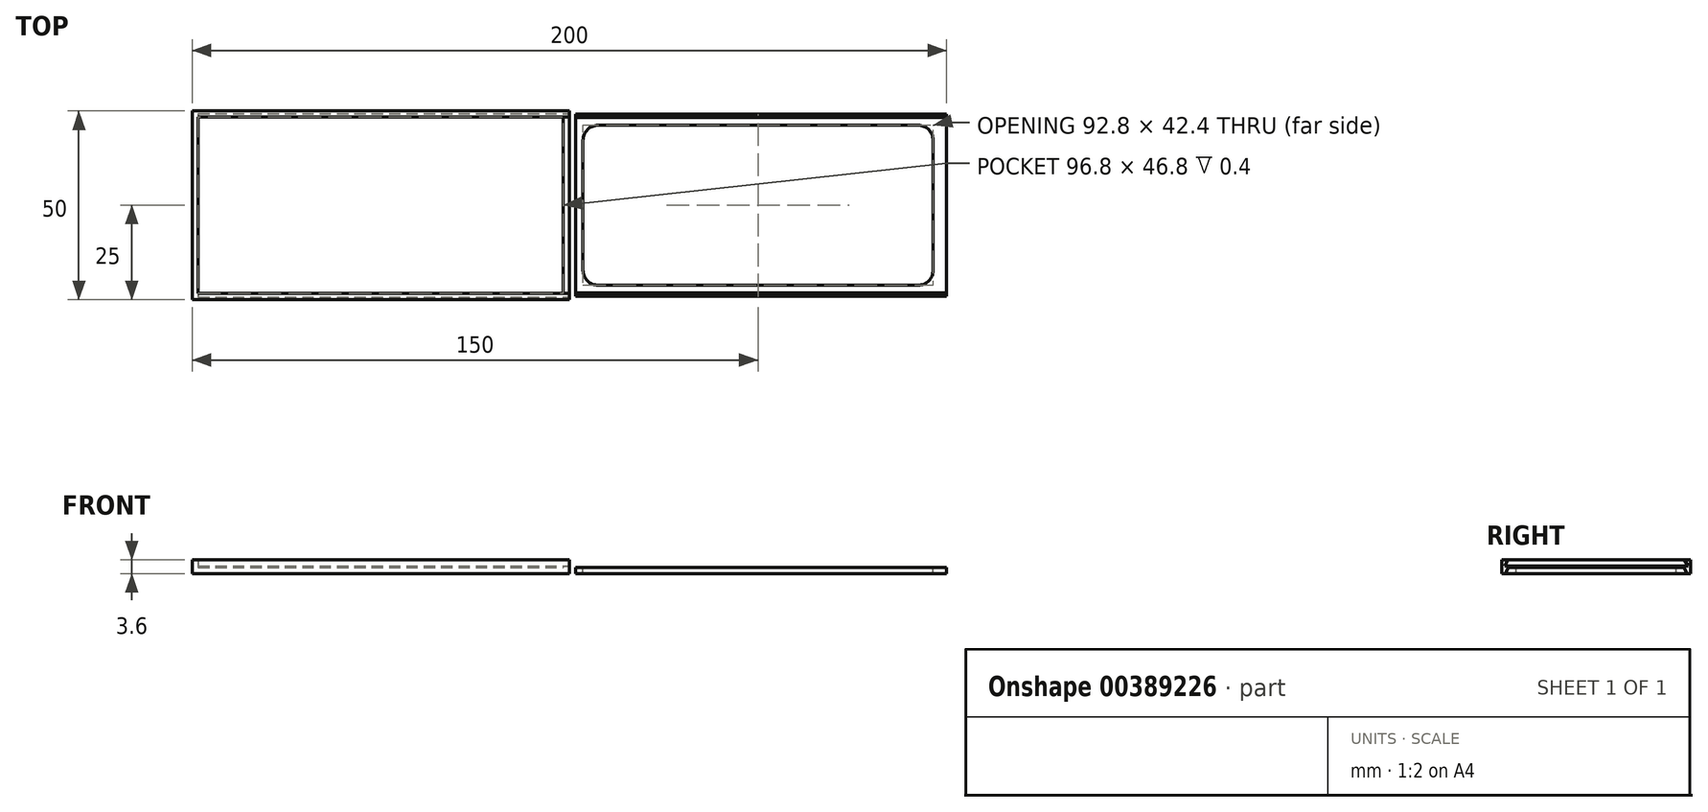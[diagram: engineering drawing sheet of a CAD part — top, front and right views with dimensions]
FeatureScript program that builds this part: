
annotation { "Feature Type Name" : "Feature", "Feature Type Description" : "" }
export const myFeature = defineFeature(function(context is Context, id is Id, definition is map)
    precondition{}
    {
        {
            assignVariable(context, id + "F0", {"name" : "Height", "anyValue" : 3.6});
        }
        {
            assignVariable(context, id + "F1", {"name" : "Length", "anyValue" : 100});
        }
        {
            assignVariable(context, id + "F2", {"name" : "WallThickness", "anyValue" : 1.6});
        }
        {
            var Q0;
            Q0=qCreatedBy(makeId("Top.planeOp"),FACE);
            var sketch = newSketch(context, id + "F3", { "sketchPlane" : qUnion([Q0])});
            skLineSegment(sketch, "E0", {"start": v(0, 0) * mm, "end": v(100, 0) * mm});
            skLineSegment(sketch, "E1", {"start": v(100, 0) * mm, "end": v(100, 50) * mm});
            skLineSegment(sketch, "E2", {"start": v(100, 50) * mm, "end": v(0, 50) * mm});
            skLineSegment(sketch, "E3", {"start": v(0, 50) * mm, "end": v(0, 0) * mm});
            skLineSegment(sketch, "E4.0", {"start": v(1.6, 1.6) * mm, "end": v(98.4, 1.6) * mm});
            skLineSegment(sketch, "E4.1", {"start": v(1.6, 48.4) * mm, "end": v(1.6, 1.6) * mm});
            skLineSegment(sketch, "E4.2", {"start": v(98.4, 48.4) * mm, "end": v(1.6, 48.4) * mm});
            skLineSegment(sketch, "E4.3", {"start": v(98.4, 1.6) * mm, "end": v(98.4, 48.4) * mm});
            skLineSegment(sketch, "E5", {"start": v(98.4, 1.6) * mm, "end": v(100, 1.6) * mm});
            skLineSegment(sketch, "E6", {"start": v(98.4, 48.4) * mm, "end": v(100, 48.4) * mm});
            skLineSegment(sketch, "E7", {"start": v(50, 50) * mm, "end": v(50, 0) * mm, "construction": true});
            skLineSegment(sketch, "E8", {"start": v(50.8, 1.6) * mm, "end": v(50.8, 48.4) * mm});
            skLineSegment(sketch, "E9.MirrorCS", {"start": v(49.2, 1.6) * mm, "end": v(49.2, 48.4) * mm});
            skSolve(sketch);
        }
        {
            var Q0;
            Q0=makeQuery(id+"F3.imprint","IMPRINT",FACE,{"disambiguationData":[TD([[makeQuery(id+"F3.imprint","IMPRINT",EDGE,{"derivedFrom":sQuery(id+"F3.wireOp",EDGE,"E0")}),1.0]])]});
            extrude(context, id + "F4", {"entities" : qUnion([Q0]), "depth" : (getVariable(context, 'Height')) * mm});
        }
        {
            var Q0;
            Q0=makeQuery(id+"F3.imprint","IMPRINT",FACE,{"disambiguationData":[TD([[makeQuery(id+"F3.imprint","IMPRINT",EDGE,{"derivedFrom":sQuery(id+"F3.wireOp",EDGE,"E4.0")}),1.0]])]});
            extrude(context, id + "F5", {"entities" : qUnion([Q0]), "operationType" : NewBodyOperationType.ADD, "depth" : (getVariable(context, 'WallThickness')) * mm});
        }
        {
            var Q0;
            Q0=makeQuery(id+"F3.imprint","IMPRINT",FACE,{"disambiguationData":[TD([[makeQuery(id+"F3.imprint","IMPRINT",EDGE,{"derivedFrom":sQuery(id+"F3.wireOp",EDGE,"E4.3")}),-1.0]])]});
            extrude(context, id + "F6", {"entities" : qUnion([Q0]), "operationType" : NewBodyOperationType.ADD, "depth" : (getVariable(context, 'Height') - getVariable(context, 'WallThickness')) * mm});
        }
        {
            var Q0;
            {var subQ0=sQuery(id+"F3.wireOp",EDGE,"E1");Q0=makeQuery(id+"F6.boolean.opBoolean","MERGE",FACE,{"derivedFrom":[makeQuery(id+"F4.opExtrude","SWEPT_FACE",FACE,{"disambiguationData":[OSD([subQ0]),TDD([makeQuery(id+"F3.imprint","IMPRINT",EDGE,{"disambiguationData":[TD([[makeQuery(id+"F3.imprint","INTERSECT",VERTEX,{"derivedFrom":[sQuery(id+"F3.wireOp",EDGE,"E0"),subQ0]}),-1.0]])],"derivedFrom":subQ0})])]}),makeQuery(id+"F4.opExtrude","SWEPT_FACE",FACE,{"disambiguationData":[OSD([subQ0]),TDD([makeQuery(id+"F3.imprint","IMPRINT",EDGE,{"disambiguationData":[TD([[makeQuery(id+"F3.imprint","INTERSECT",VERTEX,{"derivedFrom":[subQ0,sQuery(id+"F3.wireOp",EDGE,"E2")]}),1.0]])],"derivedFrom":subQ0})])]}),makeQuery(id+"F6.opExtrude","SWEPT_FACE",FACE,{"disambiguationData":[OSD([subQ0])]})]});}
            var sketch = newSketch(context, id + "F7", { "sketchPlane" : qUnion([Q0])});
            skLineSegment(sketch, "E10.0", {"start": v(1.6, 2) * mm, "end": v(48.4, 2) * mm});
            skLineSegment(sketch, "E10.1", {"start": v(0, 3.6) * mm, "end": v(1.6, 3.6) * mm, "construction": true});
            skLineSegment(sketch, "E10.2", {"start": v(48.4, 3.6) * mm, "end": v(50, 3.6) * mm, "construction": true});
            skLineSegment(sketch, "E10.3", {"start": v(50, 3.6) * mm, "end": v(50, 0) * mm, "construction": true});
            skLineSegment(sketch, "E10.4", {"start": v(0, 3.6) * mm, "end": v(0, 0) * mm, "construction": true});
            skLineSegment(sketch, "E11", {"start": v(1.6, 3.6) * mm, "end": v(0.68, 2) * mm});
            skLineSegment(sketch, "E12", {"start": v(0.68, 2) * mm, "end": v(1.6, 2) * mm});
            skPoint(sketch, "E13", {"position": v(25, 2) * mm});
            skLineSegment(sketch, "E14", {"start": v(25, 104.43) * mm, "end": v(25, 92.5) * mm, "construction": true});
            skLineSegment(sketch, "E15.MirrorCS", {"start": v(48.4, 3.6) * mm, "end": v(49.32, 2) * mm});
            skLineSegment(sketch, "E16.MirrorCS", {"start": v(49.32, 2) * mm, "end": v(48.4, 2) * mm});
            skLineSegment(sketch, "E17", {"start": v(1.6, 3.6) * mm, "end": v(48.4, 3.6) * mm});
            skLineSegment(sketch, "E18", {"start": v(0.88, 2) * mm, "end": v(1.8, 3.6) * mm});
            skLineSegment(sketch, "E19.MirrorCS", {"start": v(49.12, 2) * mm, "end": v(48.2, 3.6) * mm});
            skSolve(sketch);
        }
        {
            var Q0;
            Q0=makeQuery(id+"F7.imprint","IMPRINT",FACE,{"disambiguationData":[TD([[makeQuery(id+"F7.imprint","IMPRINT",EDGE,{"derivedFrom":sQuery(id+"F7.wireOp",EDGE,"E11")}),1.0]])]});
            var Q1;
            Q1=makeQuery(id+"F7.imprint","IMPRINT",FACE,{"disambiguationData":[TD([[makeQuery(id+"F7.imprint","IMPRINT",EDGE,{"derivedFrom":sQuery(id+"F7.wireOp",EDGE,"E15.MirrorCS")}),-1.0]])]});
            var Q2;
            {var subQ0=sQuery(id+"F7.wireOp",EDGE,"E12");var subQ3=sQuery(id+"F7.wireOp",EDGE,"E18");var subQ4=makeQuery(id+"F7.imprint","INTERSECT",VERTEX,{"derivedFrom":[subQ0,subQ3]});Q2=makeQuery(id+"F7.imprint","IMPRINT",FACE,{"disambiguationData":[TD([[makeQuery(id+"F7.imprint","IMPRINT",EDGE,{"disambiguationData":[TD([[subQ4,-1.0]])],"derivedFrom":subQ3}),-1.0]])]});}
            var Q3;
            {var subQ0=sQuery(id+"F7.wireOp",EDGE,"E16.MirrorCS");var subQ3=sQuery(id+"F7.wireOp",EDGE,"E19.MirrorCS");var subQ4=makeQuery(id+"F7.imprint","INTERSECT",VERTEX,{"derivedFrom":[subQ0,subQ3]});Q3=makeQuery(id+"F7.imprint","IMPRINT",FACE,{"disambiguationData":[TD([[makeQuery(id+"F7.imprint","IMPRINT",EDGE,{"disambiguationData":[TD([[subQ4,-1.0]])],"derivedFrom":subQ3}),1.0]])]});}
            extrude(context, id + "F8", {"entities" : qUnion([Q0, Q1, Q2, Q3]), "operationType" : NewBodyOperationType.REMOVE, "oppositeDirection" : true, "depth" : (getVariable(context, 'Length') - getVariable(context, 'WallThickness')) * mm});
        }
        {
            var Q0;
            Q0=makeQuery(id+"F7.imprint","IMPRINT",FACE,{"disambiguationData":[TD([[makeQuery(id+"F7.imprint","IMPRINT",EDGE,{"derivedFrom":sQuery(id+"F7.wireOp",EDGE,"E10.0")}),1.0]])]});
            var Q1;
            {var subQ0=sQuery(id+"F7.wireOp",EDGE,"E12");var subQ3=sQuery(id+"F7.wireOp",EDGE,"E18");var subQ4=makeQuery(id+"F7.imprint","INTERSECT",VERTEX,{"derivedFrom":[subQ0,subQ3]});Q1=makeQuery(id+"F7.imprint","IMPRINT",FACE,{"disambiguationData":[TD([[makeQuery(id+"F7.imprint","IMPRINT",EDGE,{"disambiguationData":[TD([[subQ4,-1.0]])],"derivedFrom":subQ3}),-1.0]])]});}
            var Q2;
            {var subQ0=sQuery(id+"F7.wireOp",EDGE,"E16.MirrorCS");var subQ3=sQuery(id+"F7.wireOp",EDGE,"E19.MirrorCS");var subQ4=makeQuery(id+"F7.imprint","INTERSECT",VERTEX,{"derivedFrom":[subQ0,subQ3]});Q2=makeQuery(id+"F7.imprint","IMPRINT",FACE,{"disambiguationData":[TD([[makeQuery(id+"F7.imprint","IMPRINT",EDGE,{"disambiguationData":[TD([[subQ4,-1.0]])],"derivedFrom":subQ3}),1.0]])]});}
            extrude(context, id + "F9", {"entities" : qUnion([Q0, Q1, Q2]), "depth" : (getVariable(context, 'Length')) * mm, "hasSecondDirection" : true, "secondDirectionOppositeDirection" : false, "secondDirectionDepth" : (getVariable(context, 'WallThickness')) * mm});
        }
        {
            var Q0;
            Q0=makeQuery(id+"F9.opExtrude","SWEPT_BODY",BODY,{"disambiguationData":[OSD([sQuery(id+"F7.wireOp",EDGE,"E10.0"),sQuery(id+"F7.wireOp",EDGE,"E12"),sQuery(id+"F7.wireOp",EDGE,"E16.MirrorCS"),sQuery(id+"F7.wireOp",EDGE,"E17"),sQuery(id+"F7.wireOp",EDGE,"E18"),sQuery(id+"F7.wireOp",EDGE,"E19.MirrorCS")])]});
            transform(context, id + "F10", {"entities" : qUnion([Q0]), "transformType" : TransformType.TRANSLATION_3D, "dx" : 0 * mm, "dy" : 0 * mm, "dz" : (-getVariable(context, 'Height') + getVariable(context, 'WallThickness')) * mm, "makeCopy" : false});
        }
        {
            var Q0;
            Q0=makeQuery(id+"F9.opExtrude","SWEPT_FACE",FACE,{"disambiguationData":[OSD([sQuery(id+"F7.wireOp",EDGE,"E17")])]});
            var sketch = newSketch(context, id + "F11", { "sketchPlane" : qUnion([Q0])});
            skLineSegment(sketch, "E20.0", {"start": v(200, 1.8) * mm, "end": v(200, 48.2) * mm, "construction": true});
            skLineSegment(sketch, "E20.1", {"start": v(200, 48.2) * mm, "end": v(101.6, 48.2) * mm, "construction": true});
            skLineSegment(sketch, "E20.2", {"start": v(200, 1.8) * mm, "end": v(101.6, 1.8) * mm, "construction": true});
            skLineSegment(sketch, "E20.3", {"start": v(101.6, 1.8) * mm, "end": v(101.6, 48.2) * mm, "construction": true});
            skLineSegment(sketch, "E21", {"start": v(196.4, 46.2) * mm, "end": v(196.4, 3.8) * mm});
            skLineSegment(sketch, "E22", {"start": v(196.4, 3.8) * mm, "end": v(103.6, 3.8) * mm});
            skLineSegment(sketch, "E23", {"start": v(103.6, 3.8) * mm, "end": v(103.6, 46.2) * mm});
            skLineSegment(sketch, "E24", {"start": v(103.6, 46.2) * mm, "end": v(196.4, 46.2) * mm});
            skPoint(sketch, "E25", {"position": v(196.4, 25) * mm});
            skPoint(sketch, "E26", {"position": v(200, 25) * mm});
            skSolve(sketch);
        }
        {
            var Q0;
            Q0=makeQuery(id+"F4.opExtrude","SWEPT_FACE",FACE,{"disambiguationData":[OSD([sQuery(id+"F3.wireOp",EDGE,"E0")])]});
            var sketch = newSketch(context, id + "F12", { "sketchPlane" : qUnion([Q0])});
            skLineSegment(sketch, "E27.0", {"start": v(0, 3.6) * mm, "end": v(0, 0) * mm, "construction": true});
            skLineSegment(sketch, "E27.1", {"start": v(0, 3.6) * mm, "end": v(100, 3.6) * mm, "construction": true});
            skLineSegment(sketch, "E27.2", {"start": v(100, 3.6) * mm, "end": v(100, 0) * mm, "construction": true});
            skLineSegment(sketch, "E27.3", {"start": v(0, 0) * mm, "end": v(100, 0) * mm, "construction": true});
            skLineSegment(sketch, "E28", {"start": v(0, 1.8) * mm, "end": v(100, 1.8) * mm, "construction": true});
            skLineSegment(sketch, "E29", {"start": v(50, 3.6) * mm, "end": v(50, 0) * mm, "construction": true});
            skLineSegment(sketch, "E30", {"start": v(50, 19.8) * mm, "end": v(44, 19.8) * mm});
            skLineSegment(sketch, "E31", {"start": v(44, 19.8) * mm, "end": v(44, 7.8) * mm});
            skLineSegment(sketch, "E32", {"start": v(44, 7.8) * mm, "end": v(32, 7.8) * mm});
            skLineSegment(sketch, "E33", {"start": v(32, 7.8) * mm, "end": v(32, 1.8) * mm});
            skLineSegment(sketch, "E34.MirrorCS", {"start": v(50, 19.8) * mm, "end": v(56, 19.8) * mm});
            skLineSegment(sketch, "E35.MirrorCS", {"start": v(56, 19.8) * mm, "end": v(56, 7.8) * mm});
            skLineSegment(sketch, "E36.MirrorCS", {"start": v(68, 7.8) * mm, "end": v(68, 1.8) * mm});
            skLineSegment(sketch, "E37.MirrorCS", {"start": v(56, 7.8) * mm, "end": v(68, 7.8) * mm});
            skLineSegment(sketch, "E38.MirrorCS", {"start": v(32, -4.2) * mm, "end": v(32, 1.8) * mm});
            skLineSegment(sketch, "E39.MirrorCS", {"start": v(44, -4.2) * mm, "end": v(32, -4.2) * mm});
            skLineSegment(sketch, "E40.MirrorCS", {"start": v(44, -16.2) * mm, "end": v(44, -4.2) * mm});
            skLineSegment(sketch, "E41.MirrorCS", {"start": v(50, -16.2) * mm, "end": v(44, -16.2) * mm});
            skLineSegment(sketch, "E42.MirrorCS", {"start": v(50, -16.2) * mm, "end": v(56, -16.2) * mm});
            skLineSegment(sketch, "E43.MirrorCS", {"start": v(56, -16.2) * mm, "end": v(56, -4.2) * mm});
            skLineSegment(sketch, "E44.MirrorCS", {"start": v(68, -4.2) * mm, "end": v(68, 1.8) * mm});
            skLineSegment(sketch, "E45.MirrorCS", {"start": v(56, -4.2) * mm, "end": v(68, -4.2) * mm});
            skSolve(sketch);
        }
        {
            var Q0;
            Q0 = qSketchRegion(id + "F11", true);
            extrude(context, id + "F13", {"entities" : qUnion([Q0]), "operationType" : NewBodyOperationType.REMOVE, "endBound" : BoundingType.THROUGH_ALL, "oppositeDirection" : true, "depth" : 25 * mm});
        }
        {
            var Q0;
            Q0=makeQuery(id+"F13.boolean.opBoolean","COPY",EDGE,{"derivedFrom":makeQuery(id+"F13.opExtrude","SWEPT_EDGE",EDGE,{"disambiguationData":[OSD([sQuery(id+"F11.wireOp",EDGE,"E23"),sQuery(id+"F11.wireOp",EDGE,"E24")])]})});
            var Q1;
            Q1=makeQuery(id+"F13.boolean.opBoolean","COPY",EDGE,{"derivedFrom":makeQuery(id+"F13.opExtrude","SWEPT_EDGE",EDGE,{"disambiguationData":[OSD([sQuery(id+"F11.wireOp",EDGE,"E22"),sQuery(id+"F11.wireOp",EDGE,"E23")])]})});
            var Q2;
            Q2=makeQuery(id+"F13.boolean.opBoolean","COPY",EDGE,{"derivedFrom":makeQuery(id+"F13.opExtrude","SWEPT_EDGE",EDGE,{"disambiguationData":[OSD([sQuery(id+"F11.wireOp",EDGE,"E21"),sQuery(id+"F11.wireOp",EDGE,"E22")])]})});
            var Q3;
            Q3=makeQuery(id+"F13.boolean.opBoolean","COPY",EDGE,{"derivedFrom":makeQuery(id+"F13.opExtrude","SWEPT_EDGE",EDGE,{"disambiguationData":[OSD([sQuery(id+"F11.wireOp",EDGE,"E21"),sQuery(id+"F11.wireOp",EDGE,"E24")])]})});
            fillet(context, id + "F14", {"entities" : qUnion([Q0, Q1, Q2, Q3]), "radius" : 4 * mm, "tangentPropagation" : true, "allowEdgeOverflow" : false});
        }
    });
